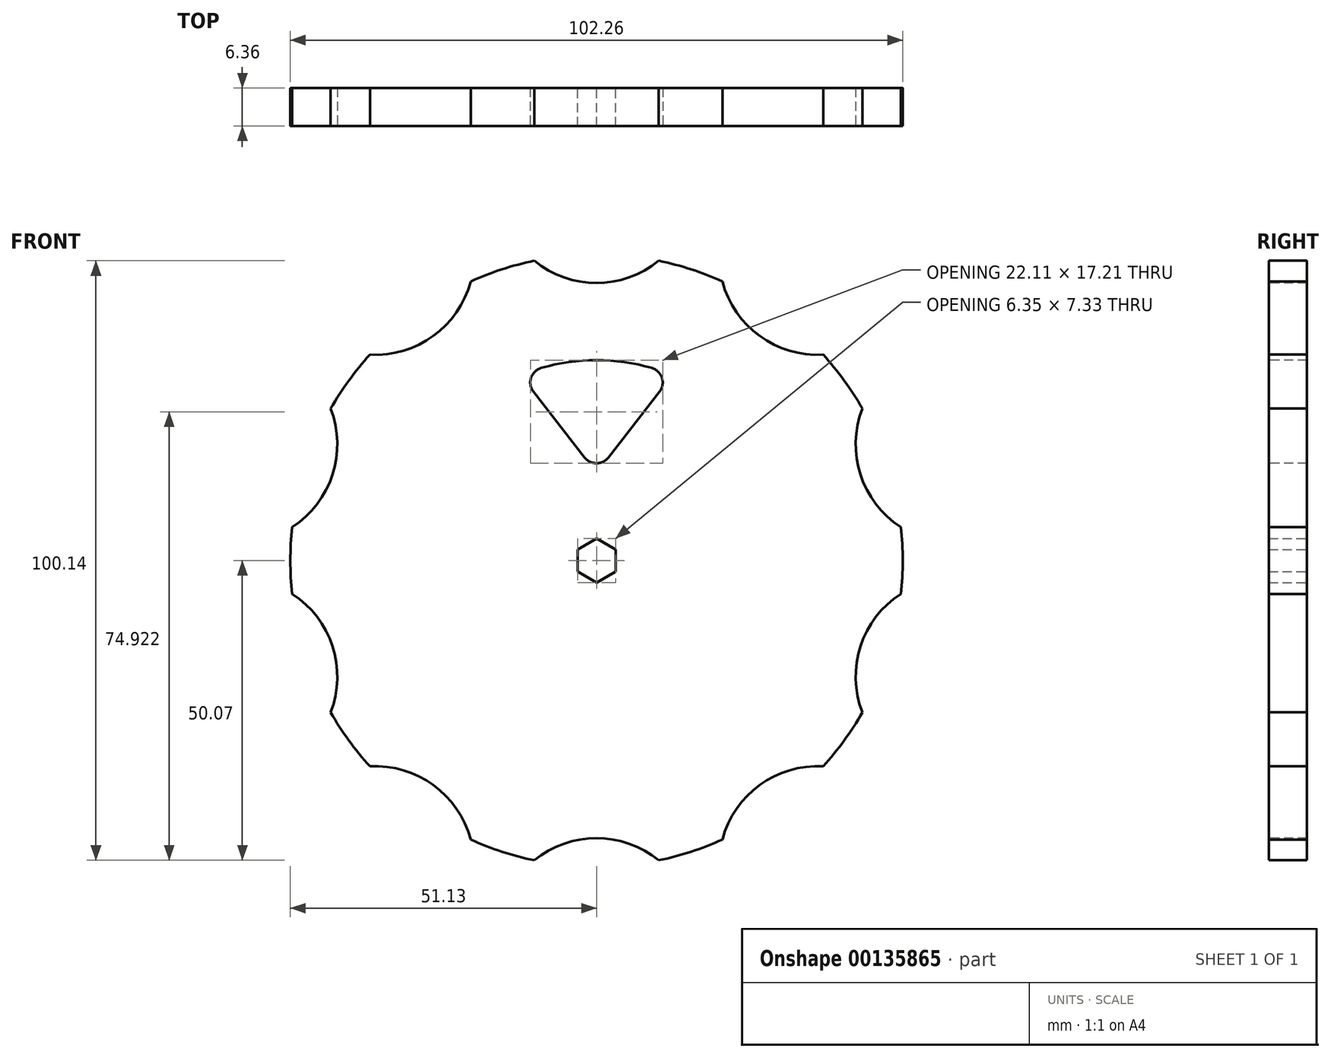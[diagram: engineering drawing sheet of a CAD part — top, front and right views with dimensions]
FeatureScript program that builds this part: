
annotation { "Feature Type Name" : "Feature", "Feature Type Description" : "" }
export const myFeature = defineFeature(function(context is Context, id is Id, definition is map)
    precondition{}
    {
        {
            var Q0;
            Q0=qCreatedBy(makeId("Front.planeOp"),FACE);
            var sketch = newSketch(context, id + "F0", { "sketchPlane" : qUnion([Q0])});
            skCircle(sketch, "E0", {"center": v(0, 0) * mm, "radius": 51.13 * mm});
            skSolve(sketch);
        }
        {
            var Q0;
            Q0=qCreatedBy(makeId("Front.planeOp"),FACE);
            var sketch = newSketch(context, id + "F1", { "sketchPlane" : qUnion([Q0])});
            skCircle(sketch, "E1.cCircle", {"center": v(0, 0) * mm, "radius": 3.18 * mm, "construction": true});
            skLineSegment(sketch, "E1.0", {"start": v(3.18, -1.83) * mm, "end": v(0, -3.67) * mm});
            skLineSegment(sketch, "E1.1", {"start": v(0, -3.67) * mm, "end": v(-3.17, -1.84) * mm});
            skLineSegment(sketch, "E1.2", {"start": v(-3.17, -1.84) * mm, "end": v(-3.18, 1.83) * mm});
            skLineSegment(sketch, "E1.3", {"start": v(-3.18, 1.83) * mm, "end": v(0, 3.67) * mm});
            skLineSegment(sketch, "E1.4", {"start": v(0, 3.67) * mm, "end": v(3.17, 1.84) * mm});
            skLineSegment(sketch, "E1.5", {"start": v(3.17, 1.84) * mm, "end": v(3.18, -1.83) * mm});
            skPoint(sketch, "E1.0.midPoint", {"position": v(1.59, -2.75) * mm});
            skSolve(sketch);
        }
        {
            var Q0;
            Q0=qCreatedBy(makeId("Front.planeOp"),FACE);
            var sketch = newSketch(context, id + "F2", { "sketchPlane" : qUnion([Q0])});
            skCircle(sketch, "E2", {"center": v(0, 62.8) * mm, "radius": 16.45 * mm});
            skCircle(sketch, "E3.1.0", {"center": v(-36.92, 50.81) * mm, "radius": 16.45 * mm});
            skCircle(sketch, "E3.2.0", {"center": v(-59.73, 19.4) * mm, "radius": 16.45 * mm});
            skCircle(sketch, "E3.3.0", {"center": v(-59.73, -19.4) * mm, "radius": 16.45 * mm});
            skCircle(sketch, "E3.4.0", {"center": v(-36.92, -50.81) * mm, "radius": 16.45 * mm});
            skCircle(sketch, "E3.5.0", {"center": v(0, -62.8) * mm, "radius": 16.45 * mm});
            skCircle(sketch, "E3.6.0", {"center": v(36.92, -50.81) * mm, "radius": 16.45 * mm});
            skCircle(sketch, "E3.7.0", {"center": v(59.73, -19.4) * mm, "radius": 16.45 * mm});
            skCircle(sketch, "E3.8.0", {"center": v(59.73, 19.4) * mm, "radius": 16.45 * mm});
            skCircle(sketch, "E3.9.0", {"center": v(36.92, 50.81) * mm, "radius": 16.45 * mm});
            skPoint(sketch, "E3.center", {"position": v(0, 0) * mm});
            skSolve(sketch);
        }
        {
            var Q0;
            Q0=qCreatedBy(makeId("Front.planeOp"),FACE);
            var sketch = newSketch(context, id + "F3", { "sketchPlane" : qUnion([Q0])});
            skLineSegment(sketch, "E4.0", {"start": v(10.52, 28.16) * mm, "end": v(2, 17.23) * mm});
            skLineSegment(sketch, "E4.1", {"start": v(-2, 17.23) * mm, "end": v(-10.52, 28.16) * mm});
            skPoint(sketch, "E4.0.midPoint", {"position": v(6.35, 22.8) * mm});
            skArc(sketch, "E5", {"start": v(-9.22, 32.16) * mm, "mid": v(0, 33.46) * mm, "end": v(9.22, 32.16) * mm});
            skPoint(sketch, "E4.cCircle.center.orphan", {"position": v(0, 29.32) * mm});
            skPoint(sketch, "E6.visualSharp", {"position": v(12.7, 30.95) * mm});
            skArc(sketch, "E6.filletArc", {"start": v(10.52, 28.16) * mm, "mid": v(10.93, 30.5) * mm, "end": v(9.22, 32.16) * mm});
            skPoint(sketch, "E7.visualSharp", {"position": v(-12.7, 30.95) * mm});
            skArc(sketch, "E7.filletArc", {"start": v(-9.22, 32.16) * mm, "mid": v(-10.93, 30.5) * mm, "end": v(-10.52, 28.16) * mm});
            skPoint(sketch, "E8.visualSharp", {"position": v(0, 14.65) * mm});
            skArc(sketch, "E8.filletArc", {"start": v(-2, 17.23) * mm, "mid": v(0, 16.25) * mm, "end": v(2, 17.23) * mm});
            skSolve(sketch);
        }
        {
            var Q0;
            Q0=makeQuery(id+"F0.imprint","IMPRINT",FACE,{"disambiguationData":[TD([[makeQuery(id+"F0.imprint","IMPRINT",EDGE,{"derivedFrom":sQuery(id+"F0.wireOp",EDGE,"E0")}),1.0]])]});
            extrude(context, id + "F4", {"entities" : qUnion([Q0]), "endBound" : BoundingType.SYMMETRIC, "depth" : 6.35 * mm});
        }
        {
            var Q0;
            Q0=makeQuery(id+"F2.imprint","IMPRINT",FACE,{"disambiguationData":[TD([[makeQuery(id+"F2.imprint","IMPRINT",EDGE,{"derivedFrom":sQuery(id+"F2.wireOp",EDGE,"E2")}),1.0]])]});
            var Q1;
            Q1=makeQuery(id+"F2.imprint","IMPRINT",FACE,{"disambiguationData":[TD([[makeQuery(id+"F2.imprint","IMPRINT",EDGE,{"derivedFrom":sQuery(id+"F2.wireOp",EDGE,"E3.9.0")}),1.0]])]});
            var Q2;
            Q2=makeQuery(id+"F2.imprint","IMPRINT",FACE,{"disambiguationData":[TD([[makeQuery(id+"F2.imprint","IMPRINT",EDGE,{"derivedFrom":sQuery(id+"F2.wireOp",EDGE,"E3.1.0")}),1.0]])]});
            var Q3;
            Q3=makeQuery(id+"F2.imprint","IMPRINT",FACE,{"disambiguationData":[TD([[makeQuery(id+"F2.imprint","IMPRINT",EDGE,{"derivedFrom":sQuery(id+"F2.wireOp",EDGE,"E3.2.0")}),1.0]])]});
            var Q4;
            Q4=makeQuery(id+"F2.imprint","IMPRINT",FACE,{"disambiguationData":[TD([[makeQuery(id+"F2.imprint","IMPRINT",EDGE,{"derivedFrom":sQuery(id+"F2.wireOp",EDGE,"E3.3.0")}),1.0]])]});
            var Q5;
            Q5=makeQuery(id+"F2.imprint","IMPRINT",FACE,{"disambiguationData":[TD([[makeQuery(id+"F2.imprint","IMPRINT",EDGE,{"derivedFrom":sQuery(id+"F2.wireOp",EDGE,"E3.4.0")}),1.0]])]});
            var Q6;
            Q6=makeQuery(id+"F2.imprint","IMPRINT",FACE,{"disambiguationData":[TD([[makeQuery(id+"F2.imprint","IMPRINT",EDGE,{"derivedFrom":sQuery(id+"F2.wireOp",EDGE,"E3.5.0")}),1.0]])]});
            var Q7;
            Q7=makeQuery(id+"F2.imprint","IMPRINT",FACE,{"disambiguationData":[TD([[makeQuery(id+"F2.imprint","IMPRINT",EDGE,{"derivedFrom":sQuery(id+"F2.wireOp",EDGE,"E3.6.0")}),1.0]])]});
            var Q8;
            Q8=makeQuery(id+"F2.imprint","IMPRINT",FACE,{"disambiguationData":[TD([[makeQuery(id+"F2.imprint","IMPRINT",EDGE,{"derivedFrom":sQuery(id+"F2.wireOp",EDGE,"E3.7.0")}),1.0]])]});
            var Q9;
            Q9=makeQuery(id+"F2.imprint","IMPRINT",FACE,{"disambiguationData":[TD([[makeQuery(id+"F2.imprint","IMPRINT",EDGE,{"derivedFrom":sQuery(id+"F2.wireOp",EDGE,"E3.8.0")}),1.0]])]});
            extrude(context, id + "F5", {"entities" : qUnion([Q0, Q1, Q2, Q3, Q4, Q5, Q6, Q7, Q8, Q9]), "operationType" : NewBodyOperationType.REMOVE, "endBound" : BoundingType.SYMMETRIC, "oppositeDirection" : true, "depth" : 25.4 * mm});
        }
        {
            var Q0;
            Q0 = qSketchRegion(id + "F1", true);
            extrude(context, id + "F6", {"entities" : qUnion([Q0]), "operationType" : NewBodyOperationType.REMOVE, "endBound" : BoundingType.SYMMETRIC, "depth" : 25.4 * mm});
        }
        {
            var Q0;
            Q0 = qSketchRegion(id + "F3", true);
            extrude(context, id + "F7", {"entities" : qUnion([Q0]), "operationType" : NewBodyOperationType.REMOVE, "endBound" : BoundingType.SYMMETRIC, "oppositeDirection" : true, "depth" : 25.4 * mm});
        }
    });
